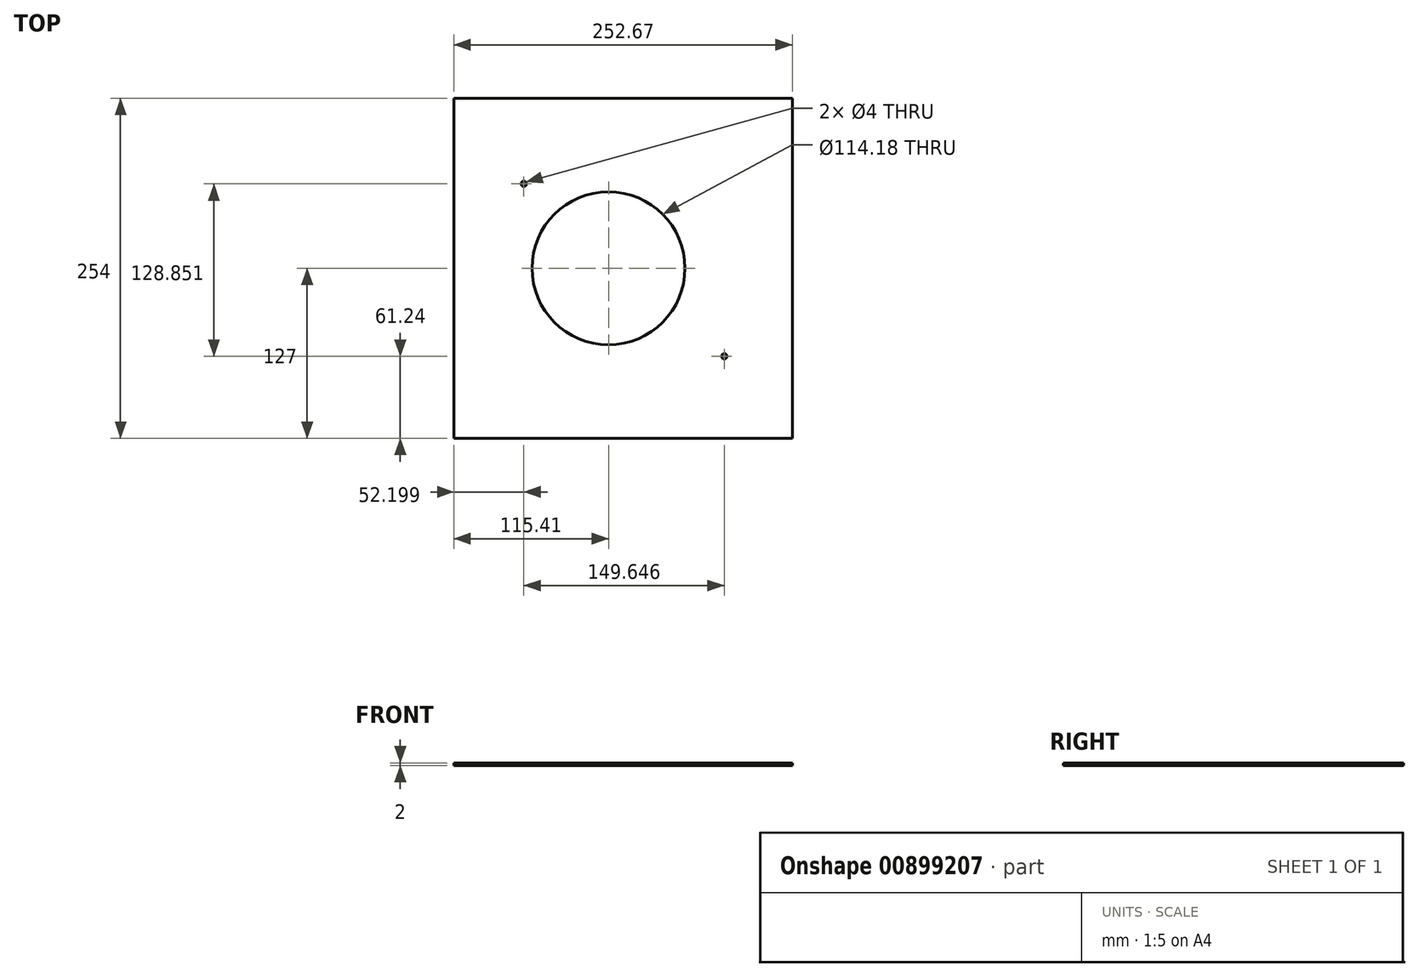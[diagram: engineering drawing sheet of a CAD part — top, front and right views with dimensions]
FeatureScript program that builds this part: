
annotation { "Feature Type Name" : "Feature", "Feature Type Description" : "" }
export const myFeature = defineFeature(function(context is Context, id is Id, definition is map)
    precondition{}
    {
        {
            var Q0;
            Q0=qCreatedBy(makeId("Top.planeOp"),FACE);
            var sketch = newSketch(context, id + "F0", { "sketchPlane" : qUnion([Q0])});
            skCircle(sketch, "E0", {"center": v(0, 0) * mm, "radius": 54.6 * mm, "construction": true});
            skArc(sketch, "E1", {"start": v(97.3, -89.96) * mm, "mid": v(0.43, -84.07) * mm, "end": v(-96.44, -89.96) * mm, "construction": true});
            skArc(sketch, "E2", {"start": v(120.48, 78.7) * mm, "mid": v(11.55, 88.9) * mm, "end": v(-97.86, 88.22) * mm, "construction": true});
            skLineSegment(sketch, "E3", {"start": v(-105.41, 80.23) * mm, "end": v(-105.41, -82.02) * mm, "construction": true});
            skLineSegment(sketch, "E4", {"start": v(127.26, 69.7) * mm, "end": v(106.2, -83.11) * mm, "construction": true});
            skArc(sketch, "E5", {"start": v(-105.41, 80.23) * mm, "mid": v(-103.23, 85.73) * mm, "end": v(-97.86, 88.22) * mm, "construction": true});
            skArc(sketch, "E6", {"start": v(120.48, 78.7) * mm, "mid": v(125.73, 75.6) * mm, "end": v(127.26, 69.7) * mm, "construction": true});
            skArc(sketch, "E7", {"start": v(106.2, -83.11) * mm, "mid": v(103.15, -88.36) * mm, "end": v(97.3, -89.96) * mm, "construction": true});
            skArc(sketch, "E8", {"start": v(-105.41, -82.02) * mm, "mid": v(-102.72, -88.01) * mm, "end": v(-96.44, -89.96) * mm, "construction": true});
            skCircle(sketch, "E9", {"center": v(-63.21, 63.1) * mm, "radius": 2 * mm});
            skCircle(sketch, "E10", {"center": v(86.44, -65.76) * mm, "radius": 2 * mm});
            skLineSegment(sketch, "E11.bottom", {"start": v(-115.41, 127) * mm, "end": v(137.26, 127) * mm});
            skLineSegment(sketch, "E11.top", {"start": v(-115.41, -127) * mm, "end": v(137.26, -127) * mm});
            skLineSegment(sketch, "E11.left", {"start": v(-115.41, 127) * mm, "end": v(-115.41, -127) * mm});
            skLineSegment(sketch, "E11.right", {"start": v(137.26, 127) * mm, "end": v(137.26, -127) * mm});
            skCircle(sketch, "E12", {"center": v(0, 0) * mm, "radius": 57.1 * mm});
            skLineSegment(sketch, "E13", {"start": v(137.26, 0) * mm, "end": v(-115.41, 0) * mm, "construction": true});
            skSolve(sketch);
        }
        {
            var Q0;
            Q0 = qSketchRegion(id + "F0", true);
            extrude(context, id + "F1", {"entities" : qUnion([Q0]), "depth" : 2 * mm, "offsetDistance" : 25 * mm});
        }
    });
